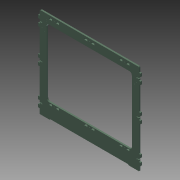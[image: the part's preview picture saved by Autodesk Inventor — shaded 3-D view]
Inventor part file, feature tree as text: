
AUTODESK INVENTOR PART (.ipt)
format: ipt  version: 2013 (Build 170138000, 138)  size: 340,992 bytes
history: native  units: mm
features: extrude x1, sketch x1
ambient origin geometry x8: Origin, YZ Plane, XZ Plane, XY Plane, X Axis, Y Axis, Z Axis, Center Point
bodies: Solid1 (feature_tree)
feature tree (2):
  extrude  "Extrusion1"  Depth=75.059196mm
  sketch  "Sketch1"  dims[d0=42.362951mm d1=75.059196mm d2=395.2mm d3=359.4mm d4=3.0mm d5=40.0mm d6=135.0deg d7=40.0mm d8=5.0mm d9=33.0mm d10=28.0mm d11=56.4mm d12=28.0mm d13=10.0mm d14=6.4mm d15=12.0mm d16=7.8mm d17=7.8mm d18=12.0mm d19=140.0mm d20=140.0mm d21=12.0mm d22=7.8mm d23=7.8mm d24=12.0mm d25=12.0mm d26=7.8mm d27=7.8mm d28=12.0mm d29=11.2mm d31=3.2mm d32=3.0mm d33=6.2mm d34=3.2mm d35=6.4mm d36=6.0mm d37=0.0mm d38=6.0mm d39=6.0mm d40=10.6mm d41=10.6mm d42=197.6mm d43=9.0mm d44=9.0mm d45=9.0mm d46=58.0mm d47=9.0mm d48=9.0mm d49=8.8mm d50=7.0mm]
